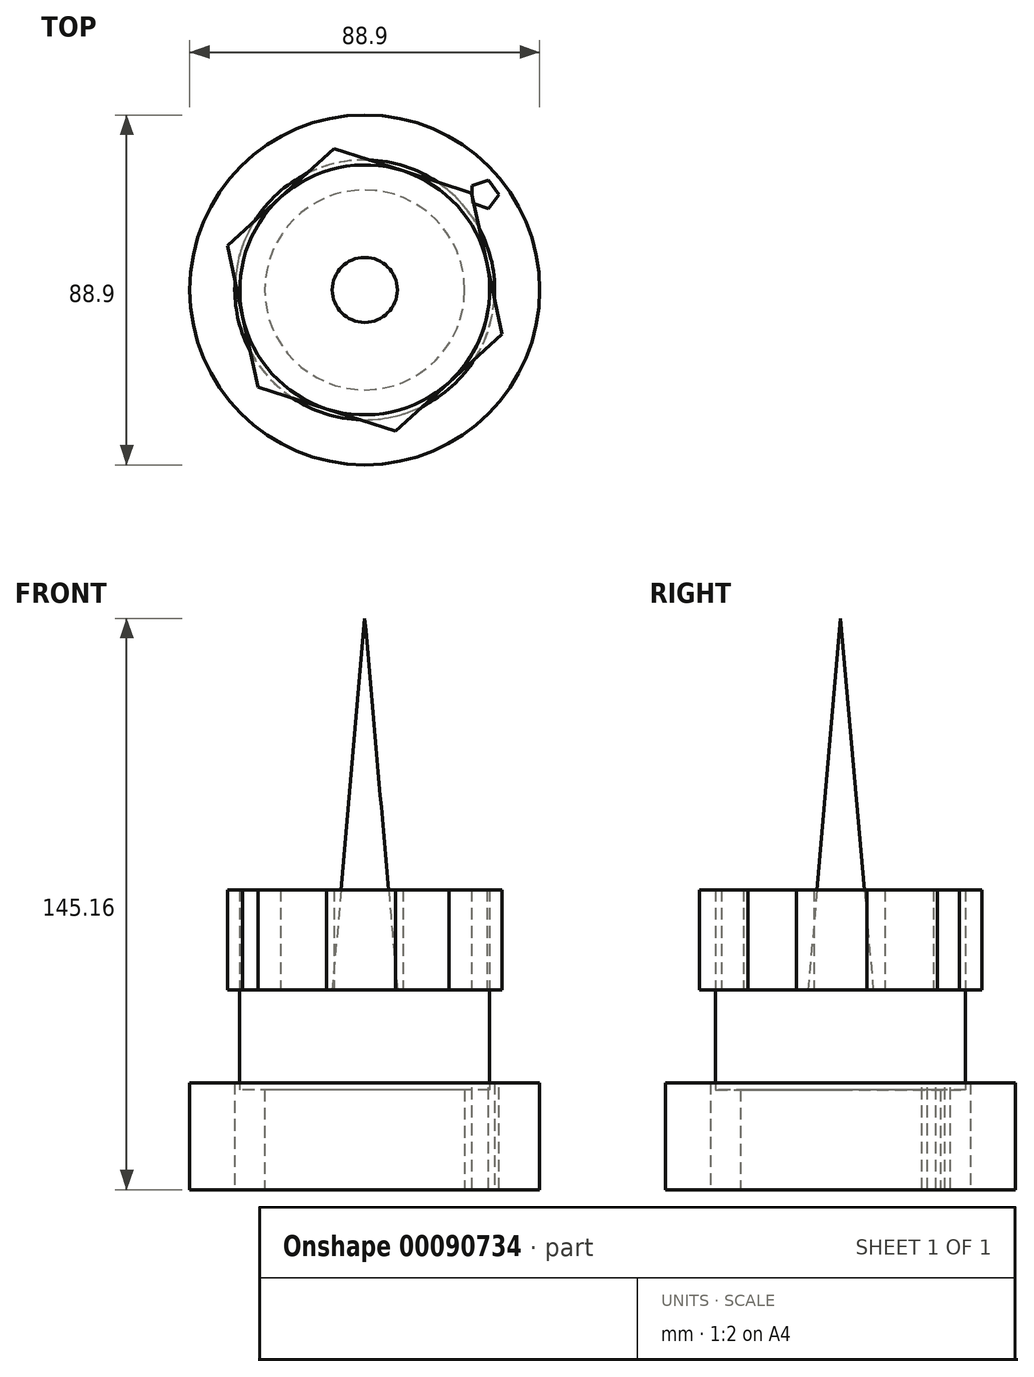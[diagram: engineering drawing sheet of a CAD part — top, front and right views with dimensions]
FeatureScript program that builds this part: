
annotation { "Feature Type Name" : "Feature", "Feature Type Description" : "" }
export const myFeature = defineFeature(function(context is Context, id is Id, definition is map)
    precondition{}
    {
        {
            var Q0;
            Q0=qCreatedBy(makeId("Top.planeOp"),FACE);
            var sketch = newSketch(context, id + "F0", { "sketchPlane" : qUnion([Q0])});
            skCircle(sketch, "E0", {"center": v(0, 0) * mm, "radius": 25.4 * mm});
            skSolve(sketch);
        }
        {
            var Q0;
            Q0 = qSketchRegion(id + "F0", true);
            var Q1;
            Q1=makeQuery(id+"F0.imprint","IMPRINT",FACE,{"disambiguationData":[TD([[makeQuery(id+"F0.imprint","IMPRINT",EDGE,{"derivedFrom":sQuery(id+"F0.wireOp",EDGE,"E0")}),1.0]])]});
            extrude(context, id + "F1", {"entities" : qUnion([Q0, Q1]), "depth" : 25.4 * mm});
        }
        {
            var Q0;
            Q0=makeQuery(id+"F1.opExtrude","CAP_FACE",FACE,{"disambiguationData":[OSD([sQuery(id+"F0.wireOp",EDGE,"E0")])],"isStart":false});
            var sketch = newSketch(context, id + "F2", { "sketchPlane" : qUnion([Q0])});
            skCircle(sketch, "E1", {"center": v(0, 0) * mm, "radius": 31.75 * mm});
            skSolve(sketch);
        }
        {
            var Q0;
            Q0 = qSketchRegion(id + "F2", true);
            var Q1;
            Q1=makeQuery(id+"F2.imprint","IMPRINT",FACE,{"disambiguationData":[TD([[makeQuery(id+"F2.imprint","IMPRINT",EDGE,{"derivedFrom":sQuery(id+"F2.wireOp",EDGE,"E1")}),1.0]])]});
            extrude(context, id + "F3", {"entities" : qUnion([Q0, Q1]), "operationType" : NewBodyOperationType.ADD, "depth" : 25.4 * mm});
        }
        {
            var Q0;
            Q0=makeQuery(id+"F3.opExtrude","CAP_FACE",FACE,{"disambiguationData":[OSD([sQuery(id+"F2.wireOp",EDGE,"E1")])],"isStart":false});
            var sketch = newSketch(context, id + "F4", { "sketchPlane" : qUnion([Q0])});
            skCircle(sketch, "E2.cCircle", {"center": v(0, 0) * mm, "radius": 31.75 * mm, "construction": true});
            skLineSegment(sketch, "E2.0", {"start": v(34.91, -11.19) * mm, "end": v(7.77, -35.83) * mm});
            skLineSegment(sketch, "E2.1", {"start": v(7.77, -35.83) * mm, "end": v(-27.15, -24.64) * mm});
            skLineSegment(sketch, "E2.2", {"start": v(-27.15, -24.64) * mm, "end": v(-34.91, 11.19) * mm});
            skLineSegment(sketch, "E2.3", {"start": v(-34.91, 11.19) * mm, "end": v(-7.77, 35.83) * mm});
            skLineSegment(sketch, "E2.4", {"start": v(-7.77, 35.83) * mm, "end": v(27.15, 24.64) * mm});
            skLineSegment(sketch, "E2.5", {"start": v(27.15, 24.64) * mm, "end": v(34.91, -11.19) * mm});
            skPoint(sketch, "E2.0.midPoint", {"position": v(21.34, -23.5) * mm});
            skSolve(sketch);
        }
        {
            var Q0;
            {var subQ0=sQuery(id+"F4.wireOp",EDGE,"E2.5");var subQ1=sQuery(id+"F4.wireOp",EDGE,"E2.4");var subQ2=makeQuery(id+"F4.imprint","INTERSECT",VERTEX,{"derivedFrom":[subQ1,subQ0]});Q0=makeQuery(id+"F4.imprint","IMPRINT",FACE,{"disambiguationData":[TD([[makeQuery(id+"F4.imprint","IMPRINT",EDGE,{"disambiguationData":[TD([[subQ2,1.0]])],"derivedFrom":subQ1}),-1.0]])]});}
            var Q1;
            {var subQ0=sQuery(id+"F4.wireOp",EDGE,"E2.5");var subQ1=sQuery(id+"F4.wireOp",EDGE,"E2.0");var subQ2=makeQuery(id+"F4.imprint","INTERSECT",VERTEX,{"derivedFrom":[subQ1,subQ0]});Q1=makeQuery(id+"F4.imprint","IMPRINT",FACE,{"disambiguationData":[TD([[makeQuery(id+"F4.imprint","IMPRINT",EDGE,{"disambiguationData":[TD([[subQ2,-1.0]])],"derivedFrom":subQ1}),-1.0]])]});}
            var Q2;
            {var subQ0=sQuery(id+"F4.wireOp",EDGE,"E2.1");var subQ1=sQuery(id+"F4.wireOp",EDGE,"E2.0");var subQ2=makeQuery(id+"F4.imprint","INTERSECT",VERTEX,{"derivedFrom":[subQ1,subQ0]});Q2=makeQuery(id+"F4.imprint","IMPRINT",FACE,{"disambiguationData":[TD([[makeQuery(id+"F4.imprint","IMPRINT",EDGE,{"disambiguationData":[TD([[subQ2,1.0]])],"derivedFrom":subQ1}),-1.0]])]});}
            var Q3;
            {var subQ0=sQuery(id+"F4.wireOp",EDGE,"E2.2");var subQ1=sQuery(id+"F4.wireOp",EDGE,"E2.1");var subQ2=makeQuery(id+"F4.imprint","INTERSECT",VERTEX,{"derivedFrom":[subQ1,subQ0]});Q3=makeQuery(id+"F4.imprint","IMPRINT",FACE,{"disambiguationData":[TD([[makeQuery(id+"F4.imprint","IMPRINT",EDGE,{"disambiguationData":[TD([[subQ2,1.0]])],"derivedFrom":subQ1}),-1.0]])]});}
            var Q4;
            {var subQ0=sQuery(id+"F4.wireOp",EDGE,"E2.3");var subQ1=sQuery(id+"F4.wireOp",EDGE,"E2.2");var subQ2=makeQuery(id+"F4.imprint","INTERSECT",VERTEX,{"derivedFrom":[subQ1,subQ0]});Q4=makeQuery(id+"F4.imprint","IMPRINT",FACE,{"disambiguationData":[TD([[makeQuery(id+"F4.imprint","IMPRINT",EDGE,{"disambiguationData":[TD([[subQ2,1.0]])],"derivedFrom":subQ1}),-1.0]])]});}
            var Q5;
            {var subQ0=sQuery(id+"F4.wireOp",EDGE,"E2.4");var subQ1=sQuery(id+"F4.wireOp",EDGE,"E2.3");var subQ2=makeQuery(id+"F4.imprint","INTERSECT",VERTEX,{"derivedFrom":[subQ1,subQ0]});Q5=makeQuery(id+"F4.imprint","IMPRINT",FACE,{"disambiguationData":[TD([[makeQuery(id+"F4.imprint","IMPRINT",EDGE,{"disambiguationData":[TD([[subQ2,1.0]])],"derivedFrom":subQ1}),-1.0]])]});}
            extrude(context, id + "F5", {"entities" : qUnion([Q0, Q1, Q2, Q3, Q4, Q5]), "depth" : 25.4 * mm});
        }
        {
            var Q0;
            Q0=qCreatedBy(makeId("Front.planeOp"),FACE);
            var sketch = newSketch(context, id + "F6", { "sketchPlane" : qUnion([Q0])});
            skLineSegment(sketch, "E3", {"start": v(0, 0) * mm, "end": v(0, 127) * mm});
            skSolve(sketch);
        }
        {
            var Q0;
            Q0=qCreatedBy(makeId("Front.planeOp"),FACE);
            var sketch = newSketch(context, id + "F7", { "sketchPlane" : qUnion([Q0])});
            skLineSegment(sketch, "E4.bottom", {"start": v(44.45, 27.16) * mm, "end": v(33.02, 27.16) * mm});
            skLineSegment(sketch, "E4.top", {"start": v(44.45, 0) * mm, "end": v(33.02, 0) * mm});
            skLineSegment(sketch, "E4.left", {"start": v(44.45, 27.16) * mm, "end": v(44.45, 0) * mm});
            skLineSegment(sketch, "E4.right", {"start": v(33.02, 27.16) * mm, "end": v(33.02, 0) * mm});
            skSolve(sketch);
        }
        {
            var Q0;
            Q0 = qSketchRegion(id + "F7", true);
            var Q1;
            Q1=makeQuery(id+"F7.imprint","IMPRINT",FACE,{"disambiguationData":[TD([[makeQuery(id+"F7.imprint","IMPRINT",EDGE,{"derivedFrom":sQuery(id+"F7.wireOp",EDGE,"E4.bottom")}),1.0]])]});
            var Q2;
            Q2=sQuery(id+"F6.wireOp",EDGE,"E3");
            revolve(context, id + "F8", {"entities" : qUnion([Q0, Q1]), "axis" : qUnion([Q2]), "revolveType" : RevolveType.FULL});
        }
        {
            var Q0;
            Q0=makeQuery(id+"F1.opExtrude","CAP_FACE",FACE,{"disambiguationData":[OSD([sQuery(id+"F0.wireOp",EDGE,"E0")])],"isStart":true});
            var sketch = newSketch(context, id + "F9", { "sketchPlane" : qUnion([Q0])});
            skCircle(sketch, "E5", {"center": v(0, 0) * mm, "radius": 12.7 * mm});
            skSolve(sketch);
        }
        {
            var Q0;
            Q0 = qSketchRegion(id + "F9", true);
            var Q1;
            Q1=makeQuery(id+"F9.imprint","IMPRINT",FACE,{"disambiguationData":[TD([[makeQuery(id+"F9.imprint","IMPRINT",EDGE,{"derivedFrom":sQuery(id+"F9.wireOp",EDGE,"E5")}),1.0]])]});
            extrude(context, id + "F10", {"entities" : qUnion([Q0, Q1]), "operationType" : NewBodyOperationType.ADD, "endBound" : BoundingType.THROUGH_ALL, "oppositeDirection" : true, "depth" : 25.4 * mm, "hasDraft" : true, "draftAngle" : 5 * degree, "draftPullDirection" : true});
        }
        {
            var Q0;
            Q0=makeQuery(id+"F8.opRevolve","SWEPT_FACE",FACE,{"disambiguationData":[OSD([sQuery(id+"F7.wireOp",EDGE,"E4.bottom")])]});
            var sketch = newSketch(context, id + "F11", { "sketchPlane" : qUnion([Q0])});
            skCircle(sketch, "E6.cCircle", {"center": v(30.3, 24.26) * mm, "radius": 3.04 * mm, "construction": true});
            skLineSegment(sketch, "E6.0", {"start": v(27.26, 22.05) * mm, "end": v(27.26, 26.46) * mm});
            skLineSegment(sketch, "E6.1", {"start": v(27.26, 26.46) * mm, "end": v(31.46, 27.83) * mm});
            skLineSegment(sketch, "E6.2", {"start": v(31.46, 27.83) * mm, "end": v(34.05, 24.26) * mm});
            skLineSegment(sketch, "E6.3", {"start": v(34.05, 24.26) * mm, "end": v(31.46, 20.69) * mm});
            skLineSegment(sketch, "E6.4", {"start": v(31.46, 20.69) * mm, "end": v(27.26, 22.05) * mm});
            skPoint(sketch, "E6.0.midPoint", {"position": v(27.26, 24.26) * mm});
            skSolve(sketch);
        }
        {
            var Q0;
            Q0=makeQuery(id+"F11.imprint","IMPRINT",FACE,{"disambiguationData":[TD([[makeQuery(id+"F11.imprint","IMPRINT",EDGE,{"derivedFrom":sQuery(id+"F11.wireOp",EDGE,"E6.0")}),-1.0]])]});
            extrude(context, id + "F12", {"entities" : qUnion([Q0]), "operationType" : NewBodyOperationType.REMOVE, "endBound" : BoundingType.THROUGH_ALL, "oppositeDirection" : true, "depth" : 25.4 * mm});
        }
    });
